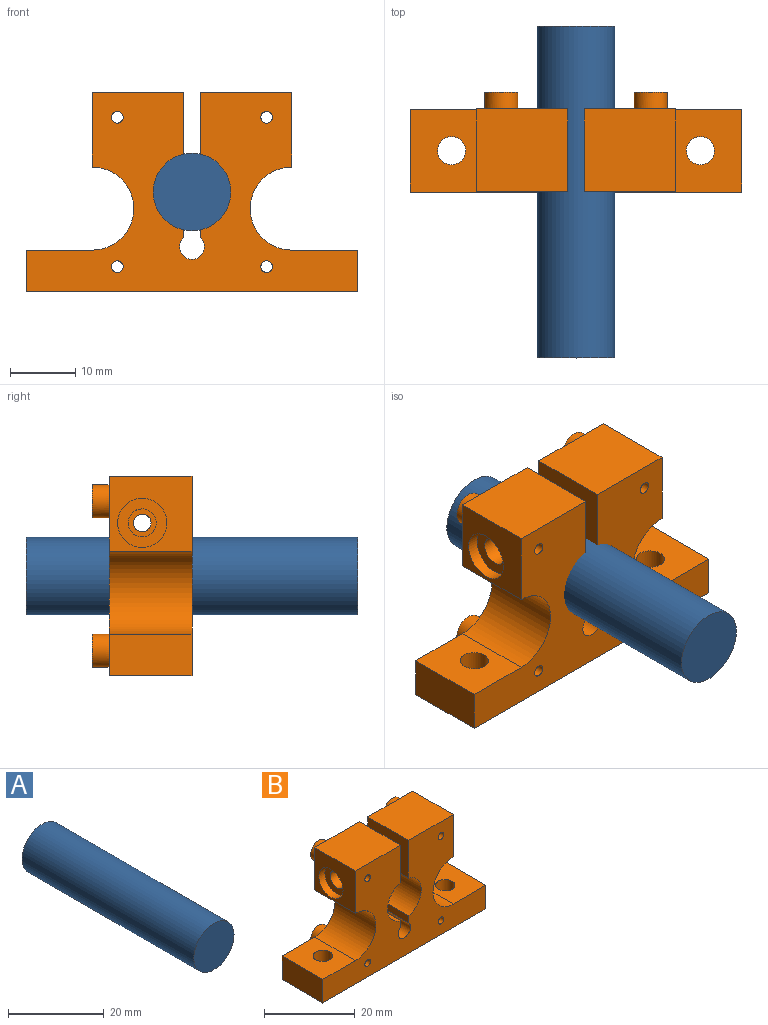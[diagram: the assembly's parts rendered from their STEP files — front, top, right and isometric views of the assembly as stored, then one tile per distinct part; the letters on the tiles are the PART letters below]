
ASSEMBLY  parts=2 mates=1
PART A: 3 faces, bbox 11.9x50.8x11.9 mm
  f0: cylinder r=5.94mm len=50.8mm, axis (0,1,0), area 1894.8mm2, adj f1,f2
  f1: plane 11.87x11.87mm, normal (0,-1,0), area 110.7mm2, adj f0
  f2: plane 11.87x11.87mm, normal (0,1,0), area 110.7mm2, adj f0
PART B: 38 faces, bbox 50.8x15.2x30.5 mm
  f0: plane 50.8x30.48mm, normal (0,-1,0), area 794.2mm2, adj f2,f3,f4,f5,f7,f9,f10,f11
  f1: plane 50.8x30.48mm, normal (0,1,0), area 723.1mm2, adj f2,f3,f4,f5,f7,f9,f10,f11
  f2: cylinder r=5.25mm len=12.7mm, axis (0,-1,0), area 176.9mm2, adj f0,f1,f25,f36
  f3: plane 12.7x11.43mm, normal (1,0,0), area 139.4mm2, adj f0,f1,f9,f27,f34
  f4: plane 12.7x11.43mm, normal (-1,0,0), area 100.5mm2, adj f0,f1,f10,f32,f33
  f5: plane 12.7x6.35mm, normal (1,0,0), area 80.6mm2, adj f0,f1,f11,f29
  f6: cylinder r=2.15mm len=6.35mm, axis (0,0,1), area 85.9mm2, adj f11,f29
  f7: plane 12.7x6.35mm, normal (-1,0,0), area 80.6mm2, adj f0,f1,f11,f28
  f8: cylinder r=2.15mm len=6.35mm, axis (0,0,1), area 85.9mm2, adj f11,f28
  f9: plane 13.97x12.7mm, normal (0,0,1), area 177.4mm2, adj f0,f1,f3,f26
  f10: plane 13.97x12.7mm, normal (0,0,1), area 177.4mm2, adj f0,f1,f4,f25
  f11: plane 50.8x12.7mm, normal (0,0,-1), area 616mm2, adj f0,f1,f5,f6,f7,f8
  f12: cylinder r=5.25mm len=12.7mm, axis (0,-1,0), area 176.9mm2, adj f0,f1,f26,f37
  f13: cylinder r=2.54mm len=5.08mm, axis (0,-1,0), area 40.5mm2, adj f1,f14
  f14: plane 5.08x5.08mm, normal (0,1,0), area 17.8mm2, adj f13,f24
  f15: cylinder r=2.54mm len=5.08mm, axis (0,-1,0), area 40.5mm2, adj f1,f16
  f16: plane 5.08x5.08mm, normal (0,1,0), area 17.8mm2, adj f15,f23
  f17: cylinder r=2.54mm len=5.08mm, axis (0,-1,0), area 40.5mm2, adj f1,f18
  f18: plane 5.08x5.08mm, normal (0,1,0), area 17.8mm2, adj f17,f22
  f19: cylinder r=2.54mm len=5.08mm, axis (0,-1,0), area 40.5mm2, adj f1,f20
  f20: plane 5.08x5.08mm, normal (0,1,0), area 17.8mm2, adj f19,f21
  f21: cylinder r=0.89mm len=15.24mm, axis (0,1,0), area 85.1mm2, adj f0,f20
  f22: cylinder r=0.89mm len=15.24mm, axis (0,1,0), area 85.1mm2, adj f0,f18
  f23: cylinder r=0.89mm len=15.24mm, axis (0,1,0), area 85.1mm2, adj f0,f16
  f24: cylinder r=0.89mm len=15.24mm, axis (0,1,0), area 85.1mm2, adj f0,f14
  f25: plane 12.7x10.15mm, normal (1,0,0), area 114.3mm2, adj f0,f1,f2,f10,f30
  f26: plane 12.7x10.15mm, normal (-1,0,0), area 123.1mm2, adj f0,f1,f9,f12,f27
  f27: cylinder r=1.35mm len=13.97mm, axis (-1,0,0), area 118.7mm2, adj f3,f26
  f28: plane 12.7x10.16mm, normal (0,0,1), area 114.5mm2, adj f0,f1,f7,f8,f33
  f29: plane 12.7x10.16mm, normal (0,0,1), area 114.5mm2, adj f0,f1,f5,f6,f34
  f30: cylinder r=2.15mm len=12.12mm, axis (-1,0,0), area 163.9mm2, adj f25,f31
  f31: plane 7.54x7.54mm, normal (-1,0,0), area 30.1mm2, adj f30,f32
  f32: cylinder r=3.77mm len=7.54mm, axis (-1,0,0), area 43.9mm2, adj f4,f31
  f33: cylinder r=6.35mm len=12.7mm, axis (0,-1,0), area 253.4mm2, adj f0,f1,f4,f28
  f34: cylinder r=6.35mm len=12.7mm, axis (0,-1,0), area 253.4mm2, adj f0,f1,f3,f29
  f35: cylinder r=1.91mm len=12.7mm, axis (0,-1,0), area 116.7mm2, adj f0,f1,f36,f37
  f36: plane 12.7x1.91mm, normal (1,0,0), area 24.3mm2, adj f0,f1,f2,f35
  f37: plane 12.7x1.91mm, normal (-1,0,0), area 24.3mm2, adj f0,f1,f12,f35
PLACE A t=(1.43,13.51,4.31)mm
PLACE B t=(1.43,-5.54,4.31)mm
MATE fastened A.f0 <-> B.f2  axis (0,1,0) through (1.43,-11.89,4.31)mm
